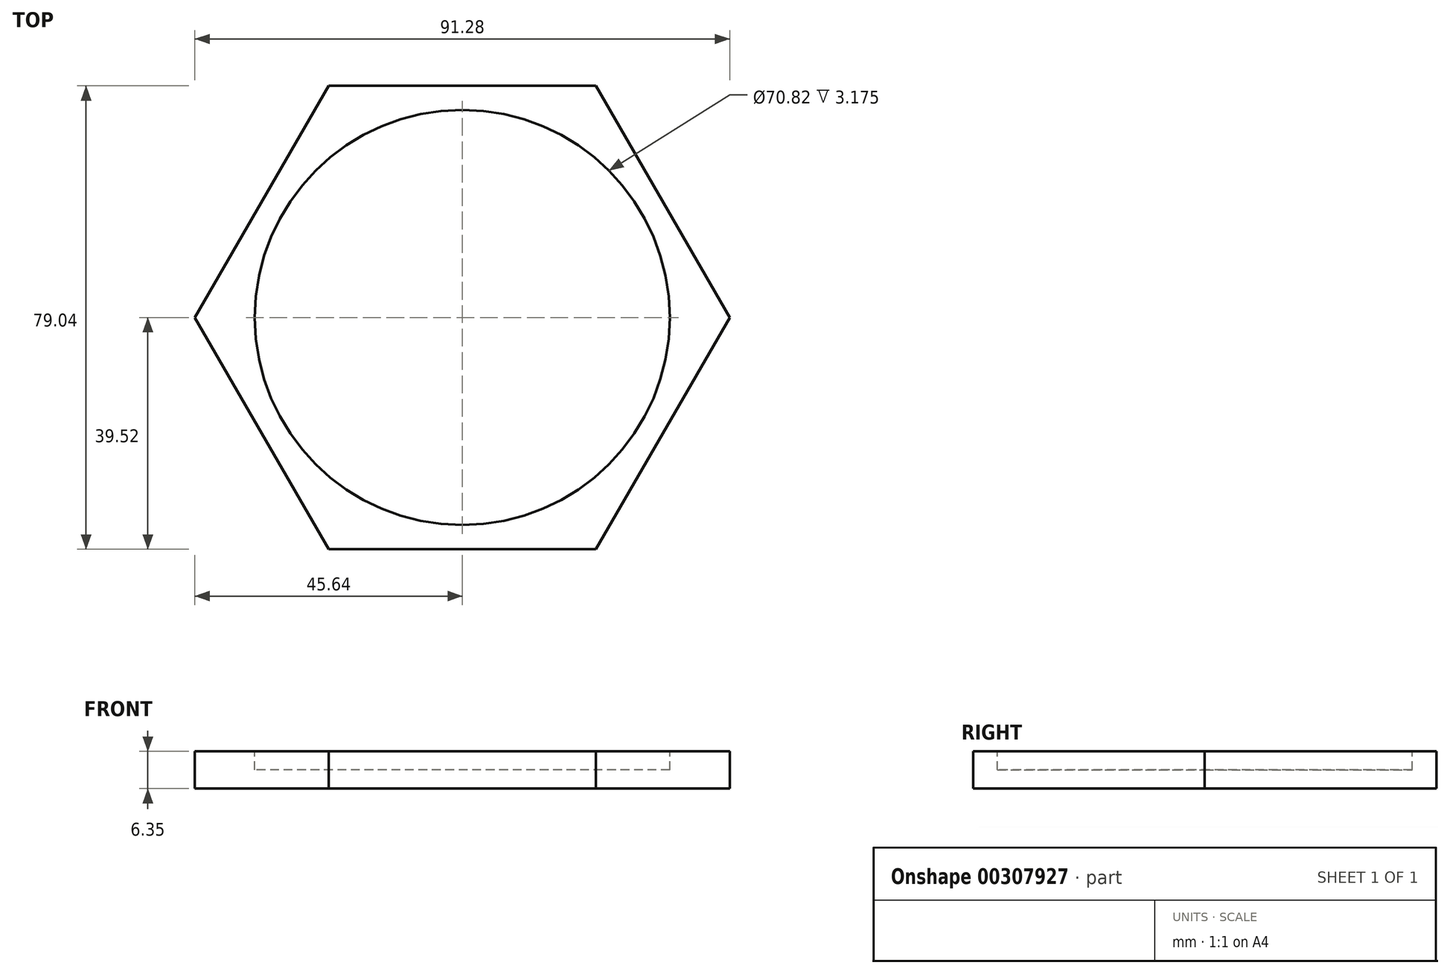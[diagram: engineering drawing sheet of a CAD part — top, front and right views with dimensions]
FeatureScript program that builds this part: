
annotation { "Feature Type Name" : "Feature", "Feature Type Description" : "" }
export const myFeature = defineFeature(function(context is Context, id is Id, definition is map)
    precondition{}
    {
        {
            var Q0;
            Q0=qCreatedBy(makeId("Top.planeOp"),FACE);
            var sketch = newSketch(context, id + "F0", { "sketchPlane" : qUnion([Q0])});
            skLineSegment(sketch, "E0", {"start": v(0, 0) * mm, "end": v(0, 39.52) * mm, "construction": true});
            skCircle(sketch, "E1.cCircle", {"center": v(0, 0) * mm, "radius": 39.52 * mm, "construction": true});
            skLineSegment(sketch, "E1.0", {"start": v(-22.82, 39.52) * mm, "end": v(22.82, 39.52) * mm});
            skLineSegment(sketch, "E1.1", {"start": v(22.82, 39.52) * mm, "end": v(45.64, 0) * mm});
            skLineSegment(sketch, "E1.2", {"start": v(45.64, 0) * mm, "end": v(22.82, -39.52) * mm});
            skLineSegment(sketch, "E1.3", {"start": v(22.82, -39.52) * mm, "end": v(-22.82, -39.52) * mm});
            skLineSegment(sketch, "E1.4", {"start": v(-22.82, -39.52) * mm, "end": v(-45.64, 0) * mm});
            skLineSegment(sketch, "E1.5", {"start": v(-45.64, 0) * mm, "end": v(-22.82, 39.52) * mm});
            skPoint(sketch, "E1.0.midPoint", {"position": v(0, 39.52) * mm});
            skSolve(sketch);
        }
        {
            var Q0;
            Q0=makeQuery(id+"F0.imprint","IMPRINT",FACE,{"disambiguationData":[TD([[makeQuery(id+"F0.imprint","IMPRINT",EDGE,{"derivedFrom":sQuery(id+"F0.wireOp",EDGE,"E1.0")}),-1.0]])]});
            extrude(context, id + "F1", {"entities" : qUnion([Q0]), "depth" : 6.35 * mm});
        }
        {
            var Q0;
            Q0=makeQuery(id+"F1.opExtrude","CAP_FACE",FACE,{"disambiguationData":[OSD([sQuery(id+"F0.wireOp",EDGE,"E1.0"),sQuery(id+"F0.wireOp",EDGE,"E1.1"),sQuery(id+"F0.wireOp",EDGE,"E1.2"),sQuery(id+"F0.wireOp",EDGE,"E1.3"),sQuery(id+"F0.wireOp",EDGE,"E1.4"),sQuery(id+"F0.wireOp",EDGE,"E1.5")])],"isStart":false});
            var sketch = newSketch(context, id + "F2", { "sketchPlane" : qUnion([Q0])});
            skCircle(sketch, "E2", {"center": v(0, 0) * mm, "radius": 35.4 * mm});
            skSolve(sketch);
        }
        {
            var Q0;
            Q0=makeQuery(id+"F2.imprint","IMPRINT",FACE,{"disambiguationData":[TD([[makeQuery(id+"F2.imprint","IMPRINT",EDGE,{"derivedFrom":sQuery(id+"F2.wireOp",EDGE,"E2")}),1.0]])]});
            extrude(context, id + "F3", {"entities" : qUnion([Q0]), "operationType" : NewBodyOperationType.REMOVE, "oppositeDirection" : true, "depth" : 3.17 * mm});
        }
    });
